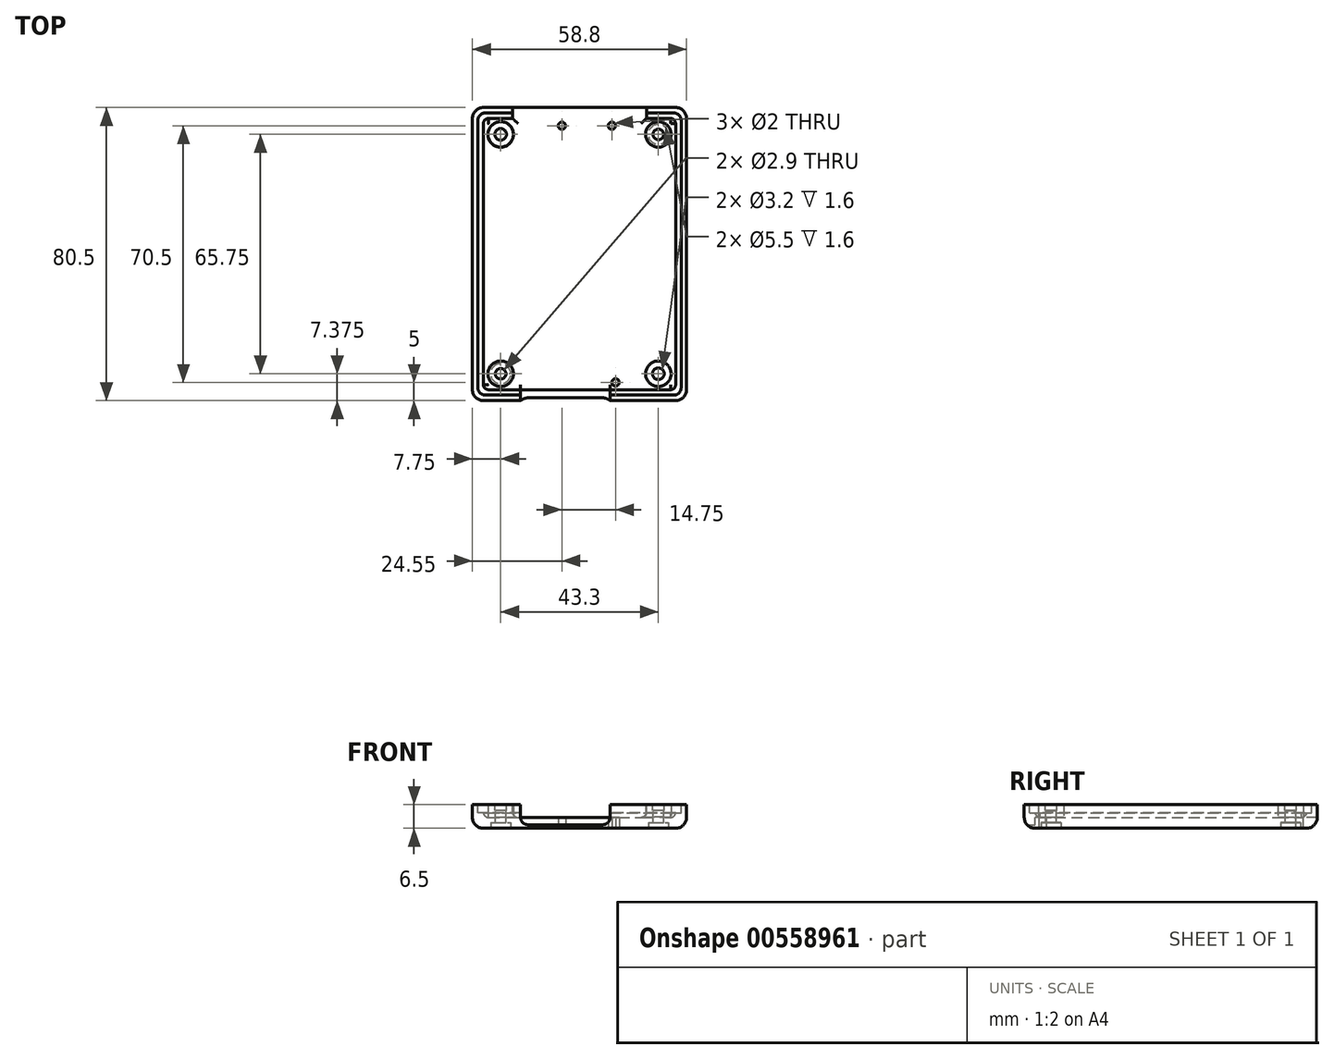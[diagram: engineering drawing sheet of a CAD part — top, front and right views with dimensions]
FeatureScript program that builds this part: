
annotation { "Feature Type Name" : "Feature", "Feature Type Description" : "" }
export const myFeature = defineFeature(function(context is Context, id is Id, definition is map)
    precondition{}
    {
        {
            var Q0;
            Q0=qCreatedBy(makeId("Top.planeOp"),FACE);
            var sketch = newSketch(context, id + "F0", { "sketchPlane" : qUnion([Q0])});
            skLineSegment(sketch, "E0.bottom", {"start": v(0, 0) * mm, "end": v(58.8, 0) * mm});
            skLineSegment(sketch, "E0.top", {"start": v(0, 80.5) * mm, "end": v(58.8, 80.5) * mm});
            skLineSegment(sketch, "E0.left", {"start": v(0, 0) * mm, "end": v(0, 80.5) * mm});
            skLineSegment(sketch, "E0.right", {"start": v(58.8, 0) * mm, "end": v(58.8, 80.5) * mm});
            skSolve(sketch);
        }
        {
            var Q0;
            Q0=makeQuery(id+"F0.imprint","IMPRINT",FACE,{"disambiguationData":[TD([[makeQuery(id+"F0.imprint","IMPRINT",EDGE,{"derivedFrom":sQuery(id+"F0.wireOp",EDGE,"E0.bottom")}),1.0]])]});
            extrude(context, id + "F1", {"entities" : qUnion([Q0]), "depth" : 6.5 * mm, "offsetDistance" : 25.4 * mm});
        }
        {
            var Q0;
            Q0=makeQuery(id+"F1.opExtrude","CAP_FACE",FACE,{"disambiguationData":[OSD([sQuery(id+"F0.wireOp",EDGE,"E0.bottom"),sQuery(id+"F0.wireOp",EDGE,"E0.top"),sQuery(id+"F0.wireOp",EDGE,"E0.left"),sQuery(id+"F0.wireOp",EDGE,"E0.right")])],"isStart":false});
            var sketch = newSketch(context, id + "F2", { "sketchPlane" : qUnion([Q0])});
            skLineSegment(sketch, "E1.bottom", {"start": v(3, 3) * mm, "end": v(55.8, 3) * mm});
            skLineSegment(sketch, "E1.top", {"start": v(3, 77.5) * mm, "end": v(55.8, 77.5) * mm});
            skLineSegment(sketch, "E1.left", {"start": v(3, 3) * mm, "end": v(3, 77.5) * mm});
            skLineSegment(sketch, "E1.right", {"start": v(55.8, 3) * mm, "end": v(55.8, 77.5) * mm});
            skSolve(sketch);
        }
        {
            var Q0;
            Q0=makeQuery(id+"F2.imprint","IMPRINT",FACE,{"disambiguationData":[TD([[makeQuery(id+"F2.imprint","IMPRINT",EDGE,{"derivedFrom":sQuery(id+"F2.wireOp",EDGE,"E1.bottom")}),1.0]])]});
            extrude(context, id + "F3", {"entities" : qUnion([Q0]), "operationType" : NewBodyOperationType.REMOVE, "oppositeDirection" : true, "depth" : 3.5 * mm, "offsetDistance" : 25.4 * mm});
        }
        {
            var Q0;
            Q0=makeQuery(id+"F3.boolean.opBoolean","COPY",FACE,{"derivedFrom":makeQuery(id+"F3.opExtrude","CAP_FACE",FACE,{"disambiguationData":[OSD([sQuery(id+"F2.wireOp",EDGE,"E1.bottom"),sQuery(id+"F2.wireOp",EDGE,"E1.top"),sQuery(id+"F2.wireOp",EDGE,"E1.left"),sQuery(id+"F2.wireOp",EDGE,"E1.right")])],"isStart":false})});
            var sketch = newSketch(context, id + "F4", { "sketchPlane" : qUnion([Q0])});
            skLineSegment(sketch, "E2.bottom", {"start": v(7.75, 7.38) * mm, "end": v(51.05, 7.38) * mm});
            skLineSegment(sketch, "E2.top", {"start": v(7.75, 73.13) * mm, "end": v(51.05, 73.13) * mm});
            skLineSegment(sketch, "E2.left", {"start": v(7.75, 7.38) * mm, "end": v(7.75, 73.13) * mm});
            skLineSegment(sketch, "E2.right", {"start": v(51.05, 7.38) * mm, "end": v(51.05, 73.13) * mm});
            skSolve(sketch);
        }
        {
            var Q0;
            Q0=makeQuery(id+"F4.imprint","IMPRINT",FACE,{"disambiguationData":[TD([[makeQuery(id+"F4.imprint","IMPRINT",EDGE,{"derivedFrom":sQuery(id+"F4.wireOp",EDGE,"E2.bottom")}),-1.0]])]});
            var sketch = newSketch(context, id + "F5", { "sketchPlane" : qUnion([Q0])});
            skCircle(sketch, "E3", {"center": v(7.75, 7.38) * mm, "radius": 3.5 * mm});
            skCircle(sketch, "E4", {"center": v(7.75, 73.13) * mm, "radius": 3.5 * mm});
            skCircle(sketch, "E5", {"center": v(51.05, 73.13) * mm, "radius": 3.5 * mm});
            skCircle(sketch, "E6", {"center": v(51.05, 7.38) * mm, "radius": 3.5 * mm});
            skSolve(sketch);
        }
        {
            var Q0;
            Q0=qSketchRegion(id+"F5",true);
            extrude(context, id + "F6", {"entities" : qUnion([Q0]), "operationType" : NewBodyOperationType.ADD, "depth" : 3.5 * mm, "offsetDistance" : 25.4 * mm});
        }
        {
            var Q0;
            Q0=makeQuery(id+"F6.opExtrude","CAP_FACE",FACE,{"disambiguationData":[OSD([sQuery(id+"F5.wireOp",EDGE,"E6")])],"isStart":false});
            var sketch = newSketch(context, id + "F7", { "sketchPlane" : qUnion([Q0])});
            skCircle(sketch, "E7", {"center": v(51.05, 7.38) * mm, "radius": 1.6 * mm});
            skSolve(sketch);
        }
        {
            var Q0;
            Q0=makeQuery(id+"F6.opExtrude","CAP_FACE",FACE,{"disambiguationData":[OSD([sQuery(id+"F5.wireOp",EDGE,"E5")])],"isStart":false});
            var sketch = newSketch(context, id + "F8", { "sketchPlane" : qUnion([Q0])});
            skCircle(sketch, "E8", {"center": v(51.05, 73.13) * mm, "radius": 1.45 * mm});
            skSolve(sketch);
        }
        {
            var Q0;
            Q0=makeQuery(id+"F6.opExtrude","CAP_FACE",FACE,{"disambiguationData":[OSD([sQuery(id+"F5.wireOp",EDGE,"E4")])],"isStart":false});
            var sketch = newSketch(context, id + "F9", { "sketchPlane" : qUnion([Q0])});
            skCircle(sketch, "E9", {"center": v(7.75, 73.13) * mm, "radius": 1.6 * mm});
            skSolve(sketch);
        }
        {
            var Q0;
            Q0=makeQuery(id+"F6.opExtrude","CAP_FACE",FACE,{"disambiguationData":[OSD([sQuery(id+"F5.wireOp",EDGE,"E3")])],"isStart":false});
            var sketch = newSketch(context, id + "F10", { "sketchPlane" : qUnion([Q0])});
            skCircle(sketch, "E10", {"center": v(7.75, 7.38) * mm, "radius": 1.45 * mm});
            skSolve(sketch);
        }
        {
            var Q0;
            Q0 = qSketchRegion(id + "F8", true);
            var Q1;
            Q1 = qSketchRegion(id + "F10", true);
            extrude(context, id + "F11", {"entities" : qUnion([Q0, Q1]), "operationType" : NewBodyOperationType.REMOVE, "endBound" : BoundingType.THROUGH_ALL, "oppositeDirection" : true, "depth" : 2.5 * mm, "offsetDistance" : 25.4 * mm});
        }
        {
            var Q0;
            Q0 = qSketchRegion(id + "F9", true);
            var Q1;
            Q1 = qSketchRegion(id + "F7", true);
            var Q2;
            Q2=qConstructionFilter(qBodyType(qCreatedBy(id+"F8",EDGE),BodyType.WIRE),ConstructionObject.NO);
            var Q3;
            Q3=qConstructionFilter(qBodyType(qCreatedBy(id+"F10",EDGE),BodyType.WIRE),ConstructionObject.NO);
            extrude(context, id + "F12", {"entities" : qUnion([Q0, Q1]), "operationType" : NewBodyOperationType.REMOVE, "surfaceEntities" : qUnion([Q2, Q3]), "oppositeDirection" : true, "depth" : 1.6 * mm, "offsetDistance" : 25 * mm});
        }
        {
            var Q0;
            Q0=makeQuery(id+"F1.opExtrude","CAP_FACE",FACE,{"disambiguationData":[OSD([sQuery(id+"F0.wireOp",EDGE,"E0.bottom"),sQuery(id+"F0.wireOp",EDGE,"E0.top"),sQuery(id+"F0.wireOp",EDGE,"E0.left"),sQuery(id+"F0.wireOp",EDGE,"E0.right")])],"isStart":false});
            var sketch = newSketch(context, id + "F13", { "sketchPlane" : qUnion([Q0])});
            skLineSegment(sketch, "E11.bottom", {"start": v(11, 80.5) * mm, "end": v(47.8, 80.5) * mm});
            skLineSegment(sketch, "E11.top", {"start": v(11, 77.5) * mm, "end": v(47.8, 77.5) * mm});
            skLineSegment(sketch, "E11.left", {"start": v(11, 80.5) * mm, "end": v(11, 77.5) * mm});
            skLineSegment(sketch, "E11.right", {"start": v(47.8, 80.5) * mm, "end": v(47.8, 77.5) * mm});
            skSolve(sketch);
        }
        {
            var Q0;
            Q0=makeQuery(id+"F13.imprint","IMPRINT",FACE,{"disambiguationData":[TD([[makeQuery(id+"F13.imprint","IMPRINT",EDGE,{"derivedFrom":sQuery(id+"F13.wireOp",EDGE,"E11.bottom")}),-1.0]])]});
            extrude(context, id + "F14", {"entities" : qUnion([Q0]), "operationType" : NewBodyOperationType.REMOVE, "oppositeDirection" : true, "depth" : 3.5 * mm, "offsetDistance" : 25.4 * mm});
        }
        {
            var Q0;
            Q0=makeQuery(id+"F1.opExtrude","CAP_FACE",FACE,{"disambiguationData":[OSD([sQuery(id+"F0.wireOp",EDGE,"E0.bottom"),sQuery(id+"F0.wireOp",EDGE,"E0.top"),sQuery(id+"F0.wireOp",EDGE,"E0.left"),sQuery(id+"F0.wireOp",EDGE,"E0.right")])],"isStart":false});
            var sketch = newSketch(context, id + "F15", { "sketchPlane" : qUnion([Q0])});
            skLineSegment(sketch, "E12.bottom", {"start": v(13.2, 0) * mm, "end": v(37.8, 0) * mm});
            skLineSegment(sketch, "E12.top", {"start": v(13.2, 3) * mm, "end": v(37.8, 3) * mm});
            skLineSegment(sketch, "E12.left", {"start": v(13.2, 0) * mm, "end": v(13.2, 3) * mm});
            skLineSegment(sketch, "E12.right", {"start": v(37.8, 0) * mm, "end": v(37.8, 3) * mm});
            skSolve(sketch);
        }
        {
            var Q0;
            Q0=qSketchRegion(id+"F15",true);
            extrude(context, id + "F16", {"entities" : qUnion([Q0]), "operationType" : NewBodyOperationType.REMOVE, "oppositeDirection" : true, "depth" : 5.5 * mm, "offsetDistance" : 25.4 * mm});
        }
        {
            var Q0;
            {var subQ0=sQuery(id+"F0.wireOp",EDGE,"E0.right");var subQ1=sQuery(id+"F0.wireOp",EDGE,"E0.top");var subQ2=sQuery(id+"F0.wireOp",EDGE,"E0.bottom");Q0=makeQuery(id+"F16.boolean.opBoolean","SPLIT",FACE,{"disambiguationData":[TD([makeQuery(id+"F1.opExtrude","SWEPT_FACE",FACE,{"disambiguationData":[OSD([subQ0])]})])],"derivedFrom":makeQuery(id+"F1.opExtrude","CAP_FACE",FACE,{"disambiguationData":[OSD([subQ2,subQ1,sQuery(id+"F0.wireOp",EDGE,"E0.left"),subQ0])],"isStart":false})});}
            var sketch = newSketch(context, id + "F17", { "sketchPlane" : qUnion([Q0])});
            skLineSegment(sketch, "E13", {"start": v(37.8, 1.5) * mm, "end": v(58.8, 1.5) * mm, "construction": true});
            skLineSegment(sketch, "E14", {"start": v(47.8, 79) * mm, "end": v(58.8, 79) * mm, "construction": true});
            skLineSegment(sketch, "E15", {"start": v(58.8, 80.5) * mm, "end": v(55.8, 77.5) * mm, "construction": true});
            skLineSegment(sketch, "E16", {"start": v(55.8, 3) * mm, "end": v(58.8, 0) * mm, "construction": true});
            skLineSegment(sketch, "E17", {"start": v(47.8, 77.5) * mm, "end": v(47.8, 79) * mm});
            skLineSegment(sketch, "E18", {"start": v(57.3, 79) * mm, "end": v(57.3, 1.5) * mm});
            skLineSegment(sketch, "E19", {"start": v(57.3, 1.5) * mm, "end": v(37.8, 1.5) * mm});
            skLineSegment(sketch, "E20", {"start": v(37.8, 3) * mm, "end": v(55.8, 3) * mm});
            skLineSegment(sketch, "E21", {"start": v(55.8, 77.5) * mm, "end": v(47.8, 77.5) * mm});
            skLineSegment(sketch, "E22", {"start": v(47.8, 79) * mm, "end": v(57.3, 79) * mm});
            skLineSegment(sketch, "E23", {"start": v(55.8, 3) * mm, "end": v(55.8, 77.5) * mm});
            skLineSegment(sketch, "E24", {"start": v(37.8, 3) * mm, "end": v(37.8, 1.5) * mm});
            skSolve(sketch);
        }
        {
            var Q0;
            {var subQ0=sQuery(id+"F0.wireOp",EDGE,"E0.left");var subQ1=sQuery(id+"F0.wireOp",EDGE,"E0.top");var subQ2=sQuery(id+"F0.wireOp",EDGE,"E0.bottom");Q0=makeQuery(id+"F16.boolean.opBoolean","SPLIT",FACE,{"disambiguationData":[TD([makeQuery(id+"F1.opExtrude","SWEPT_FACE",FACE,{"disambiguationData":[OSD([subQ0])]})])],"derivedFrom":makeQuery(id+"F1.opExtrude","CAP_FACE",FACE,{"disambiguationData":[OSD([subQ2,subQ1,subQ0,sQuery(id+"F0.wireOp",EDGE,"E0.right")])],"isStart":false})});}
            var sketch = newSketch(context, id + "F18", { "sketchPlane" : qUnion([Q0])});
            skLineSegment(sketch, "E25", {"start": v(11, 79) * mm, "end": v(0, 79) * mm, "construction": true});
            skLineSegment(sketch, "E26", {"start": v(0, 79) * mm, "end": v(0, 80.5) * mm, "construction": true});
            skLineSegment(sketch, "E27", {"start": v(0, 80.5) * mm, "end": v(3, 77.5) * mm, "construction": true});
            skLineSegment(sketch, "E28", {"start": v(13.2, 1.5) * mm, "end": v(0, 1.5) * mm, "construction": true});
            skLineSegment(sketch, "E29", {"start": v(0, 1.5) * mm, "end": v(0, 0) * mm, "construction": true});
            skLineSegment(sketch, "E30", {"start": v(0, 0) * mm, "end": v(3, 3) * mm, "construction": true});
            skLineSegment(sketch, "E31", {"start": v(13.2, 1.5) * mm, "end": v(1.5, 1.5) * mm});
            skLineSegment(sketch, "E32", {"start": v(1.5, 1.5) * mm, "end": v(1.5, 79) * mm});
            skLineSegment(sketch, "E33", {"start": v(1.5, 79) * mm, "end": v(11, 79) * mm});
            skLineSegment(sketch, "E34", {"start": v(11, 77.5) * mm, "end": v(11, 79) * mm});
            skLineSegment(sketch, "E35", {"start": v(11, 77.5) * mm, "end": v(3, 77.5) * mm});
            skLineSegment(sketch, "E36", {"start": v(3, 77.5) * mm, "end": v(3, 3) * mm});
            skLineSegment(sketch, "E37", {"start": v(3, 3) * mm, "end": v(13.2, 3) * mm});
            skLineSegment(sketch, "E38", {"start": v(13.2, 3) * mm, "end": v(13.2, 1.5) * mm});
            skSolve(sketch);
        }
        {
            var Q0;
            Q0=qSketchRegion(id+"F17",true);
            var Q1;
            Q1=qSketchRegion(id+"F18",true);
            var Q2;
            Q2=sQuery(id+"F17.wireOp",EDGE,"E23");
            var Q3;
            Q3=sQuery(id+"F17.wireOp",EDGE,"E20");
            var Q4;
            Q4=sQuery(id+"F17.wireOp",EDGE,"E19");
            var Q5;
            Q5=sQuery(id+"F17.wireOp",EDGE,"E18");
            var Q6;
            Q6=sQuery(id+"F17.wireOp",EDGE,"E22");
            var Q7;
            Q7=sQuery(id+"F17.wireOp",EDGE,"E17");
            var Q8;
            Q8=sQuery(id+"F17.wireOp",EDGE,"E21");
            var Q9;
            Q9=sQuery(id+"F17.wireOp",EDGE,"E24");
            extrude(context, id + "F19", {"entities" : qUnion([Q0, Q1]), "operationType" : NewBodyOperationType.REMOVE, "surfaceEntities" : qUnion([Q2, Q3, Q4, Q5, Q6, Q7, Q8, Q9]), "oppositeDirection" : true, "depth" : 2.2 * mm, "offsetDistance" : 25 * mm});
        }
        {
            var Q0;
            Q0=makeQuery(id+"F1.opExtrude","CAP_FACE",FACE,{"disambiguationData":[OSD([sQuery(id+"F0.wireOp",EDGE,"E0.bottom"),sQuery(id+"F0.wireOp",EDGE,"E0.top"),sQuery(id+"F0.wireOp",EDGE,"E0.left"),sQuery(id+"F0.wireOp",EDGE,"E0.right")])],"isStart":true});
            var sketch = newSketch(context, id + "F20", { "sketchPlane" : qUnion([Q0])});
            skCircle(sketch, "E39", {"center": v(39.3, -5) * mm, "radius": 1 * mm});
            skCircle(sketch, "E40", {"center": v(38.3, -75.5) * mm, "radius": 1 * mm});
            skCircle(sketch, "E41", {"center": v(24.55, -75.5) * mm, "radius": 1 * mm});
            skSolve(sketch);
        }
        {
            var Q0;
            Q0 = qSketchRegion(id + "F20", true);
            extrude(context, id + "F21", {"entities" : qUnion([Q0]), "operationType" : NewBodyOperationType.REMOVE, "endBound" : BoundingType.THROUGH_ALL, "oppositeDirection" : true, "depth" : 25 * mm, "offsetDistance" : 25 * mm});
        }
        {
            var Q0;
            Q0=makeQuery(id+"F1.opExtrude","SWEPT_EDGE",EDGE,{"disambiguationData":[OSD([sQuery(id+"F0.wireOp",EDGE,"E0.bottom"),sQuery(id+"F0.wireOp",EDGE,"E0.left")])]});
            var Q1;
            Q1=makeQuery(id+"F1.opExtrude","CAP_EDGE",EDGE,{"disambiguationData":[OSD([sQuery(id+"F0.wireOp",EDGE,"E0.bottom")])],"isStart":true});
            var Q2;
            Q2=makeQuery(id+"F1.opExtrude","SWEPT_EDGE",EDGE,{"disambiguationData":[OSD([sQuery(id+"F0.wireOp",EDGE,"E0.bottom"),sQuery(id+"F0.wireOp",EDGE,"E0.right")])]});
            var Q3;
            Q3=makeQuery(id+"F1.opExtrude","CAP_EDGE",EDGE,{"disambiguationData":[OSD([sQuery(id+"F0.wireOp",EDGE,"E0.left")])],"isStart":true});
            var Q4;
            Q4=makeQuery(id+"F1.opExtrude","SWEPT_EDGE",EDGE,{"disambiguationData":[OSD([sQuery(id+"F0.wireOp",EDGE,"E0.top"),sQuery(id+"F0.wireOp",EDGE,"E0.left")])]});
            var Q5;
            Q5=makeQuery(id+"F1.opExtrude","CAP_EDGE",EDGE,{"disambiguationData":[OSD([sQuery(id+"F0.wireOp",EDGE,"E0.top")])],"isStart":true});
            var Q6;
            Q6=makeQuery(id+"F1.opExtrude","SWEPT_EDGE",EDGE,{"disambiguationData":[OSD([sQuery(id+"F0.wireOp",EDGE,"E0.top"),sQuery(id+"F0.wireOp",EDGE,"E0.right")])]});
            var Q7;
            Q7=makeQuery(id+"F1.opExtrude","CAP_EDGE",EDGE,{"disambiguationData":[OSD([sQuery(id+"F0.wireOp",EDGE,"E0.right")])],"isStart":true});
            fillet(context, id + "F22", {"entities" : qUnion([Q0, Q1, Q2, Q3, Q4, Q5, Q6, Q7]), "radius" : 3 * mm, "tangentPropagation" : true, "allowEdgeOverflow" : false});
        }
        {
            var Q0;
            Q0=makeQuery(id+"F3.boolean.opBoolean","COPY",EDGE,{"derivedFrom":makeQuery(id+"F3.opExtrude","SWEPT_EDGE",EDGE,{"disambiguationData":[OSD([sQuery(id+"F2.wireOp",EDGE,"E1.bottom"),sQuery(id+"F2.wireOp",EDGE,"E1.right")])]})});
            var Q1;
            Q1=makeQuery(id+"F3.boolean.opBoolean","COPY",EDGE,{"derivedFrom":makeQuery(id+"F3.opExtrude","SWEPT_EDGE",EDGE,{"disambiguationData":[OSD([sQuery(id+"F2.wireOp",EDGE,"E1.bottom"),sQuery(id+"F2.wireOp",EDGE,"E1.left")])]})});
            var Q2;
            Q2=makeQuery(id+"F3.boolean.opBoolean","COPY",EDGE,{"derivedFrom":makeQuery(id+"F3.opExtrude","SWEPT_EDGE",EDGE,{"disambiguationData":[OSD([sQuery(id+"F2.wireOp",EDGE,"E1.top"),sQuery(id+"F2.wireOp",EDGE,"E1.left")])]})});
            var Q3;
            Q3=makeQuery(id+"F3.boolean.opBoolean","COPY",EDGE,{"derivedFrom":makeQuery(id+"F3.opExtrude","SWEPT_EDGE",EDGE,{"disambiguationData":[OSD([sQuery(id+"F2.wireOp",EDGE,"E1.top"),sQuery(id+"F2.wireOp",EDGE,"E1.right")])]})});
            var Q4;
            Q4=makeQuery(id+"F3.boolean.opBoolean","COPY",EDGE,{"derivedFrom":makeQuery(id+"F3.opExtrude","CAP_EDGE",EDGE,{"disambiguationData":[OSD([sQuery(id+"F2.wireOp",EDGE,"E1.right")])],"isStart":false})});
            var Q5;
            Q5=makeQuery(id+"F3.boolean.opBoolean","COPY",EDGE,{"derivedFrom":makeQuery(id+"F3.opExtrude","CAP_EDGE",EDGE,{"disambiguationData":[OSD([sQuery(id+"F2.wireOp",EDGE,"E1.bottom")])],"isStart":false})});
            var Q6;
            Q6=makeQuery(id+"F3.boolean.opBoolean","COPY",EDGE,{"derivedFrom":makeQuery(id+"F3.opExtrude","CAP_EDGE",EDGE,{"disambiguationData":[OSD([sQuery(id+"F2.wireOp",EDGE,"E1.left")])],"isStart":false})});
            var Q7;
            Q7=makeQuery(id+"F3.boolean.opBoolean","COPY",EDGE,{"derivedFrom":makeQuery(id+"F3.opExtrude","CAP_EDGE",EDGE,{"disambiguationData":[OSD([sQuery(id+"F2.wireOp",EDGE,"E1.top")])],"isStart":false})});
            var Q8;
            Q8=makeQuery(id+"F19.opExtrude","SWEPT_EDGE",EDGE,{"disambiguationData":[OSD([sQuery(id+"F17.wireOp",EDGE,"E20"),sQuery(id+"F17.wireOp",EDGE,"E23")])]});
            var Q9;
            Q9=makeQuery(id+"F19.opExtrude","SWEPT_EDGE",EDGE,{"disambiguationData":[OSD([sQuery(id+"F17.wireOp",EDGE,"E21"),sQuery(id+"F17.wireOp",EDGE,"E23")])]});
            var Q10;
            Q10=makeQuery(id+"F19.opExtrude","SWEPT_EDGE",EDGE,{"disambiguationData":[OSD([sQuery(id+"F18.wireOp",EDGE,"E36"),sQuery(id+"F18.wireOp",EDGE,"E37")])]});
            var Q11;
            Q11=makeQuery(id+"F19.opExtrude","SWEPT_EDGE",EDGE,{"disambiguationData":[OSD([sQuery(id+"F18.wireOp",EDGE,"E35"),sQuery(id+"F18.wireOp",EDGE,"E36")])]});
            fillet(context, id + "F23", {"entities" : qUnion([Q0, Q1, Q2, Q3, Q4, Q5, Q6, Q7, Q8, Q9, Q10, Q11]), "radius" : 1.4 * mm, "tangentPropagation" : true, "allowEdgeOverflow" : false});
        }
        {
            var Q0;
            Q0=makeQuery(id+"F19.boolean.opBoolean","COPY",EDGE,{"derivedFrom":makeQuery(id+"F19.opExtrude","SWEPT_EDGE",EDGE,{"disambiguationData":[OSD([sQuery(id+"F17.wireOp",EDGE,"E18"),sQuery(id+"F17.wireOp",EDGE,"E22")])]})});
            var Q1;
            Q1=makeQuery(id+"F19.boolean.opBoolean","COPY",EDGE,{"derivedFrom":makeQuery(id+"F19.opExtrude","SWEPT_EDGE",EDGE,{"disambiguationData":[OSD([sQuery(id+"F17.wireOp",EDGE,"E18"),sQuery(id+"F17.wireOp",EDGE,"E19")])]})});
            var Q2;
            Q2=makeQuery(id+"F19.boolean.opBoolean","COPY",EDGE,{"derivedFrom":makeQuery(id+"F19.opExtrude","SWEPT_EDGE",EDGE,{"disambiguationData":[OSD([sQuery(id+"F18.wireOp",EDGE,"E31"),sQuery(id+"F18.wireOp",EDGE,"E32")])]})});
            var Q3;
            Q3=makeQuery(id+"F19.boolean.opBoolean","COPY",EDGE,{"derivedFrom":makeQuery(id+"F19.opExtrude","SWEPT_EDGE",EDGE,{"disambiguationData":[OSD([sQuery(id+"F18.wireOp",EDGE,"E32"),sQuery(id+"F18.wireOp",EDGE,"E33")])]})});
            fillet(context, id + "F24", {"entities" : qUnion([Q0, Q1, Q2, Q3]), "radius" : 2 * mm, "tangentPropagation" : true, "allowEdgeOverflow" : false});
        }
        {
            var Q0;
            Q0=makeQuery(id+"F14.boolean.opBoolean","COPY",EDGE,{"derivedFrom":makeQuery(id+"F14.opExtrude","CAP_EDGE",EDGE,{"disambiguationData":[OSD([sQuery(id+"F13.wireOp",EDGE,"E11.left")])],"isStart":false})});
            var Q1;
            Q1=makeQuery(id+"F14.boolean.opBoolean","COPY",EDGE,{"derivedFrom":makeQuery(id+"F14.opExtrude","CAP_EDGE",EDGE,{"disambiguationData":[OSD([sQuery(id+"F13.wireOp",EDGE,"E11.right")])],"isStart":false})});
            fillet(context, id + "F25", {"entities" : qUnion([Q0, Q1]), "radius" : 1.5 * mm, "tangentPropagation" : true, "allowEdgeOverflow" : false});
        }
        {
            var Q0;
            Q0=makeQuery(id+"F16.boolean.opBoolean","COPY",EDGE,{"derivedFrom":makeQuery(id+"F16.opExtrude","CAP_EDGE",EDGE,{"disambiguationData":[OSD([sQuery(id+"F15.wireOp",EDGE,"E12.left")])],"isStart":false})});
            var Q1;
            Q1=makeQuery(id+"F16.boolean.opBoolean","COPY",EDGE,{"derivedFrom":makeQuery(id+"F16.opExtrude","CAP_EDGE",EDGE,{"disambiguationData":[OSD([sQuery(id+"F15.wireOp",EDGE,"E12.right")])],"isStart":false})});
            fillet(context, id + "F26", {"entities" : qUnion([Q0, Q1]), "radius" : 2 * mm, "tangentPropagation" : true, "allowEdgeOverflow" : false});
        }
        {
            var Q0;
            Q0=makeQuery(id+"F1.opExtrude","CAP_FACE",FACE,{"disambiguationData":[OSD([sQuery(id+"F0.wireOp",EDGE,"E0.bottom"),sQuery(id+"F0.wireOp",EDGE,"E0.top"),sQuery(id+"F0.wireOp",EDGE,"E0.left"),sQuery(id+"F0.wireOp",EDGE,"E0.right")])],"isStart":true});
            var sketch = newSketch(context, id + "F27", { "sketchPlane" : qUnion([Q0])});
            skCircle(sketch, "E42", {"center": v(51.05, -73.12) * mm, "radius": 2.75 * mm});
            skCircle(sketch, "E43", {"center": v(7.75, -7.38) * mm, "radius": 2.75 * mm});
            skSolve(sketch);
        }
        {
            var Q0;
            Q0=qSketchRegion(id+"F27",true);
            extrude(context, id + "F28", {"entities" : qUnion([Q0]), "operationType" : NewBodyOperationType.REMOVE, "oppositeDirection" : true, "depth" : 1.6 * mm, "offsetDistance" : 25 * mm});
        }
    });
